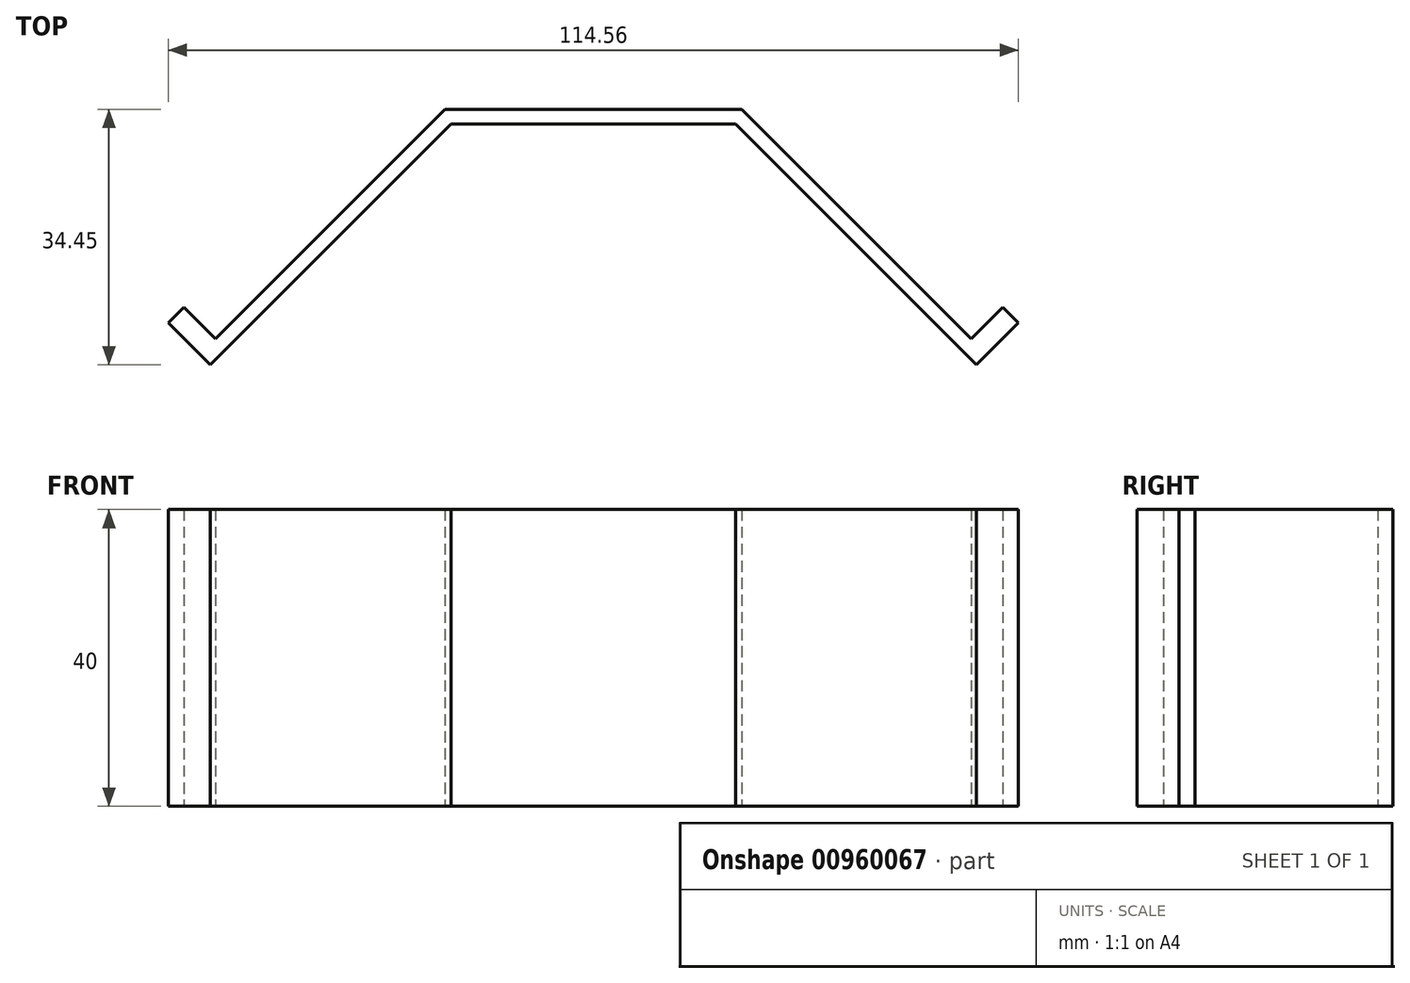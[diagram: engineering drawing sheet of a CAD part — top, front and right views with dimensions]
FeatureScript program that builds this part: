
annotation { "Feature Type Name" : "Feature", "Feature Type Description" : "" }
export const myFeature = defineFeature(function(context is Context, id is Id, definition is map)
    precondition{}
    {
        {
            var Q0;
            Q0=qCreatedBy(makeId("Top.planeOp"),FACE);
            var sketch = newSketch(context, id + "F0", { "sketchPlane" : qUnion([Q0])});
            skLineSegment(sketch, "E0", {"start": v(0, 20) * mm, "end": v(-50.91, -30.91) * mm});
            skLineSegment(sketch, "E1", {"start": v(-50.91, -30.91) * mm, "end": v(-55.15, -26.67) * mm});
            skLineSegment(sketch, "E2", {"start": v(0, 0) * mm, "end": v(-20, 0) * mm});
            skLineSegment(sketch, "E3.MirrorCS", {"start": v(0, 0) * mm, "end": v(20, 0) * mm});
            skLineSegment(sketch, "E4.MirrorCS", {"start": v(0, 20) * mm, "end": v(50.91, -30.91) * mm});
            skLineSegment(sketch, "E5.MirrorCS", {"start": v(50.91, -30.91) * mm, "end": v(55.15, -26.67) * mm});
            skLineSegment(sketch, "E6", {"start": v(-55.15, -26.67) * mm, "end": v(-57.28, -28.8) * mm});
            skPoint(sketch, "E6.endSnap0", {"position": v(-53.03, -28.8) * mm});
            skLineSegment(sketch, "E7", {"start": v(-57.28, -28.8) * mm, "end": v(-51.62, -34.45) * mm});
            skLineSegment(sketch, "E8", {"start": v(-51.62, -34.45) * mm, "end": v(-19.17, -2) * mm});
            skLineSegment(sketch, "E9", {"start": v(-19.17, -2) * mm, "end": v(0, -2) * mm});
            skLineSegment(sketch, "E10.MirrorCS", {"start": v(19.17, -2) * mm, "end": v(0, -2) * mm});
            skLineSegment(sketch, "E11.MirrorCS", {"start": v(51.62, -34.45) * mm, "end": v(19.17, -2) * mm});
            skLineSegment(sketch, "E12.MirrorCS", {"start": v(57.28, -28.8) * mm, "end": v(51.62, -34.45) * mm});
            skLineSegment(sketch, "E13.MirrorCS", {"start": v(55.15, -26.67) * mm, "end": v(57.28, -28.8) * mm});
            skSolve(sketch);
        }
        {
            var Q0;
            {var subQ3=sQuery(id+"F0.wireOp",EDGE,"E1");Q0=makeQuery(id+"F0.imprint","IMPRINT",FACE,{"disambiguationData":[TD([[makeQuery(id+"F0.imprint","IMPRINT",EDGE,{"derivedFrom":subQ3}),1.0]])]});}
            extrude(context, id + "F1", {"entities" : qUnion([Q0]), "depth" : 40 * mm, "offsetDistance" : 25 * mm});
        }
    });
